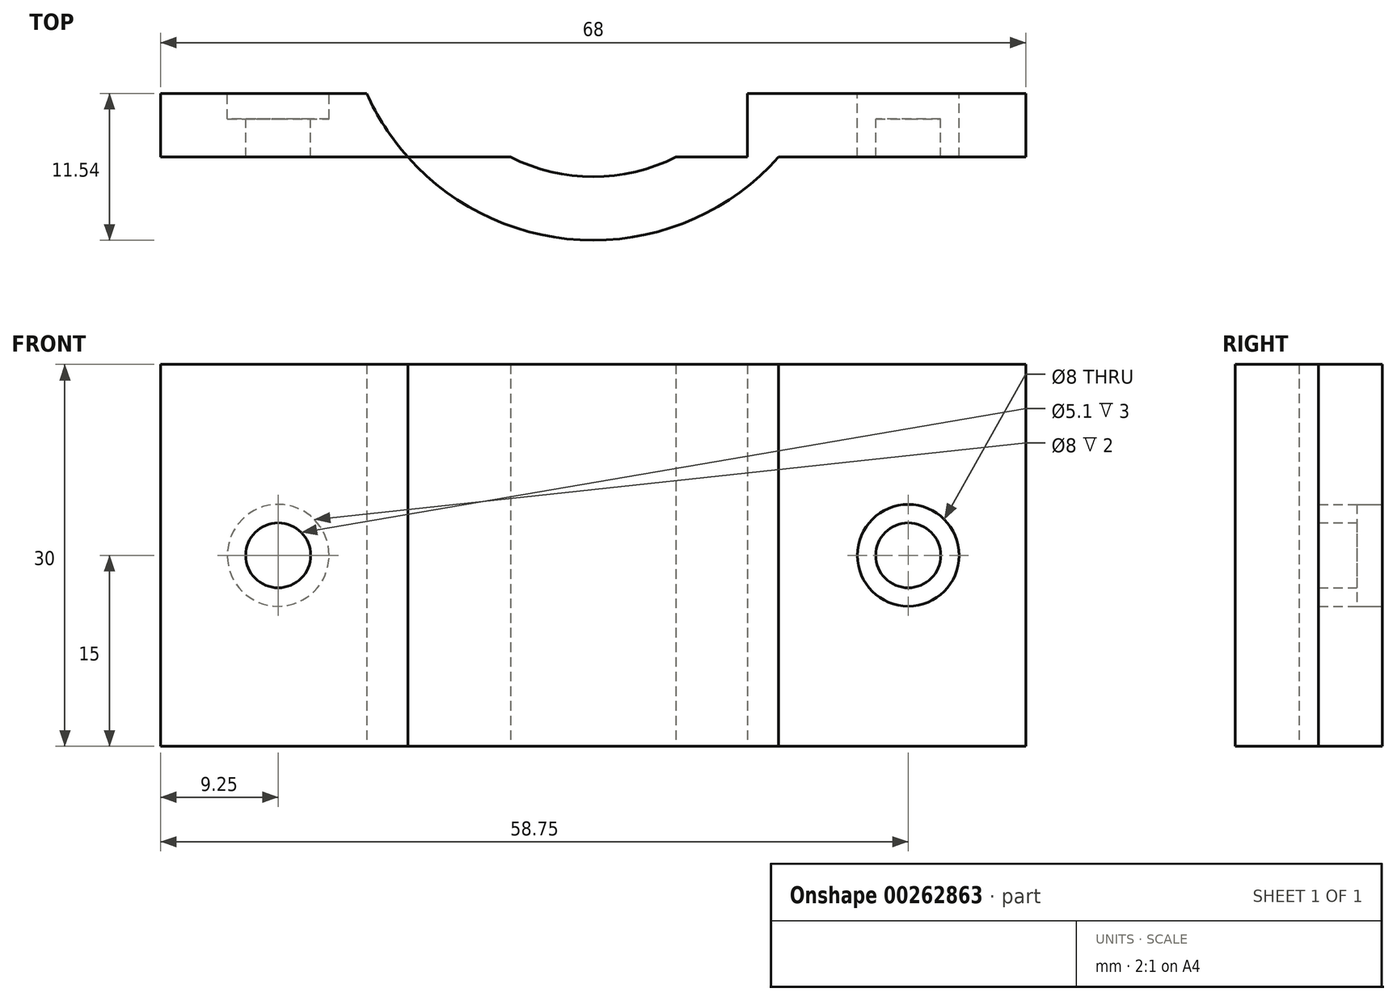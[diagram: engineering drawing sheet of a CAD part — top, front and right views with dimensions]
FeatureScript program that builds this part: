
annotation { "Feature Type Name" : "Feature", "Feature Type Description" : "" }
export const myFeature = defineFeature(function(context is Context, id is Id, definition is map)
    precondition{}
    {
        {
            var Q0;
            Q0=qCreatedBy(makeId("Top.planeOp"),FACE);
            var sketch = newSketch(context, id + "F0", { "sketchPlane" : qUnion([Q0])});
            skLineSegment(sketch, "E0.bottom", {"start": v(-34, 0) * mm, "end": v(34, 0) * mm});
            skLineSegment(sketch, "E0.top", {"start": v(-34, 5) * mm, "end": v(34, 5) * mm});
            skLineSegment(sketch, "E0.left", {"start": v(-34, 0) * mm, "end": v(-34, 5) * mm});
            skLineSegment(sketch, "E0.right", {"start": v(34, 0) * mm, "end": v(34, 5) * mm});
            skCircle(sketch, "E1", {"center": v(0, 12.96) * mm, "radius": 14.5 * mm});
            skCircle(sketch, "E2", {"center": v(0, 12.96) * mm, "radius": 19.5 * mm});
            skPoint(sketch, "E3", {"position": v(-6.5, 0) * mm});
            skPoint(sketch, "E4", {"position": v(6.5, 0) * mm});
            skLineSegment(sketch, "E5.bottom", {"start": v(-12.12, 0) * mm, "end": v(12.12, 0) * mm});
            skLineSegment(sketch, "E5.top", {"start": v(-12.12, 20) * mm, "end": v(12.12, 20) * mm});
            skLineSegment(sketch, "E5.left", {"start": v(-12.12, 0) * mm, "end": v(-12.12, 20) * mm});
            skLineSegment(sketch, "E5.right", {"start": v(12.12, 0) * mm, "end": v(12.12, 20) * mm});
            skPoint(sketch, "E6", {"position": v(-12.12, 5) * mm});
            skSolve(sketch);
        }
        {
            var Q0;
            {var subQ0=sQuery(id+"F0.wireOp",EDGE,"E0.left");Q0=makeQuery(id+"F0.imprint","IMPRINT",FACE,{"disambiguationData":[TD([[makeQuery(id+"F0.imprint","IMPRINT",EDGE,{"derivedFrom":subQ0}),-1.0]])]});}
            var Q1;
            {var subQ1=sQuery(id+"F0.wireOp",EDGE,"E0.bottom");var subQ3=sQuery(id+"F0.wireOp",EDGE,"E2");var subQ4=makeQuery(id+"F0.imprint","INTERSECT",VERTEX,{"disambiguationData":[OD(0.0)],"derivedFrom":[subQ1,subQ3]});Q1=makeQuery(id+"F0.imprint","IMPRINT",FACE,{"disambiguationData":[TD([[makeQuery(id+"F0.imprint","IMPRINT",EDGE,{"disambiguationData":[TD([[subQ4,1.0]])],"derivedFrom":subQ3}),1.0]])]});}
            var Q2;
            {var subQ0=sQuery(id+"F0.wireOp",EDGE,"E2");var subQ1=sQuery(id+"F0.wireOp",EDGE,"E0.top");var subQ2=makeQuery(id+"F0.imprint","INTERSECT",VERTEX,{"disambiguationData":[OD(0.0)],"derivedFrom":[subQ1,subQ0]});Q2=makeQuery(id+"F0.imprint","IMPRINT",FACE,{"disambiguationData":[TD([[makeQuery(id+"F0.imprint","IMPRINT",EDGE,{"disambiguationData":[TD([[subQ2,1.0]])],"derivedFrom":subQ0}),1.0]])]});}
            var Q3;
            {var subQ1=sQuery(id+"F0.wireOp",EDGE,"E0.bottom");var subQ3=sQuery(id+"F0.wireOp",EDGE,"E2");var subQ4=makeQuery(id+"F0.imprint","INTERSECT",VERTEX,{"disambiguationData":[OD(1.0)],"derivedFrom":[subQ1,subQ3]});Q3=makeQuery(id+"F0.imprint","IMPRINT",FACE,{"disambiguationData":[TD([[makeQuery(id+"F0.imprint","IMPRINT",EDGE,{"disambiguationData":[TD([[subQ4,-1.0]])],"derivedFrom":subQ3}),1.0]])]});}
            var Q4;
            {var subQ0=sQuery(id+"F0.wireOp",EDGE,"E0.right");Q4=makeQuery(id+"F0.imprint","IMPRINT",FACE,{"disambiguationData":[TD([[makeQuery(id+"F0.imprint","IMPRINT",EDGE,{"derivedFrom":subQ0}),1.0]])]});}
            extrude(context, id + "F1", {"entities" : qUnion([Q0, Q1, Q2, Q3, Q4]), "depth" : 30 * mm});
        }
        {
            var Q0;
            {var subQ0=sQuery(id+"F0.wireOp",EDGE,"E0.top");Q0=makeQuery(id+"F1.opExtrude","SWEPT_FACE",FACE,{"disambiguationData":[OSD([subQ0]),TDD([makeQuery(id+"F0.imprint","IMPRINT",EDGE,{"disambiguationData":[TD([[makeQuery(id+"F0.imprint","INTERSECT",VERTEX,{"derivedFrom":[subQ0,sQuery(id+"F0.wireOp",EDGE,"E0.left")]}),-1.0]])],"derivedFrom":subQ0})])]});}
            var sketch = newSketch(context, id + "F2", { "sketchPlane" : qUnion([Q0])});
            skCircle(sketch, "E7", {"center": v(24.75, 15) * mm, "radius": 2.55 * mm});
            skLineSegment(sketch, "E8.bottom", {"start": v(34, 0) * mm, "end": v(17.8, 0) * mm});
            skLineSegment(sketch, "E8.top", {"start": v(34, 30) * mm, "end": v(17.8, 30) * mm});
            skLineSegment(sketch, "E8.left", {"start": v(34, 0) * mm, "end": v(34, 30) * mm});
            skLineSegment(sketch, "E8.right", {"start": v(17.8, 0) * mm, "end": v(17.8, 30) * mm});
            skCircle(sketch, "E9.MirrorC", {"center": v(-24.75, 15) * mm, "radius": 2.55 * mm});
            skCircle(sketch, "E10", {"center": v(24.75, 15) * mm, "radius": 4 * mm});
            skCircle(sketch, "E11", {"center": v(-24.75, 15) * mm, "radius": 4 * mm});
            skSolve(sketch);
        }
        {
            var Q0;
            Q0=makeQuery(id+"F2.imprint","IMPRINT",FACE,{"disambiguationData":[TD([[makeQuery(id+"F2.imprint","IMPRINT",EDGE,{"derivedFrom":sQuery(id+"F2.wireOp",EDGE,"E9.MirrorC")}),-1.0]])]});
            var Q1;
            Q1=makeQuery(id+"F2.imprint","IMPRINT",FACE,{"disambiguationData":[TD([[makeQuery(id+"F2.imprint","IMPRINT",EDGE,{"derivedFrom":sQuery(id+"F2.wireOp",EDGE,"E7")}),1.0]])]});
            extrude(context, id + "F3", {"entities" : qUnion([Q0, Q1]), "operationType" : NewBodyOperationType.REMOVE, "oppositeDirection" : true, "depth" : 6 * mm});
        }
        {
            var Q0;
            Q0=makeQuery(id+"F2.imprint","IMPRINT",FACE,{"disambiguationData":[TD([[makeQuery(id+"F2.imprint","IMPRINT",EDGE,{"derivedFrom":sQuery(id+"F2.wireOp",EDGE,"E7")}),-1.0]])]});
            var Q1;
            Q1=makeQuery(id+"F2.imprint","IMPRINT",FACE,{"disambiguationData":[TD([[makeQuery(id+"F2.imprint","IMPRINT",EDGE,{"derivedFrom":sQuery(id+"F2.wireOp",EDGE,"E9.MirrorC")}),1.0]])]});
            extrude(context, id + "F4", {"entities" : qUnion([Q0, Q1]), "operationType" : NewBodyOperationType.REMOVE, "oppositeDirection" : true, "depth" : 2 * mm});
        }
    });
